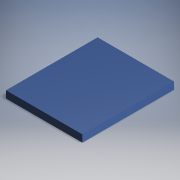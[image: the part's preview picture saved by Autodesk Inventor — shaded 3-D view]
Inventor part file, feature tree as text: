
AUTODESK INVENTOR PART (.ipt)
format: ipt  version: 2018 (Build 220112000, 112)  size: 107,008 bytes
history: native  units: in
note: dims shown in document units (in); Inventor stores cm internally (conversion verified against a paired STEP export)
features: extrude x1, sketch x1
ambient origin geometry x8: Origin, YZ Plane, XZ Plane, XY Plane, X Axis, Y Axis, Z Axis, Center Point
bodies: Solid1 (feature_tree)
feature tree (2):
  extrude  "Extrusion1"  Depth=1.9173in
  sketch  "Sketch1"  dims[d0=1.5984in d1=1.9173in d2=0.1496in d3=0.0in]
